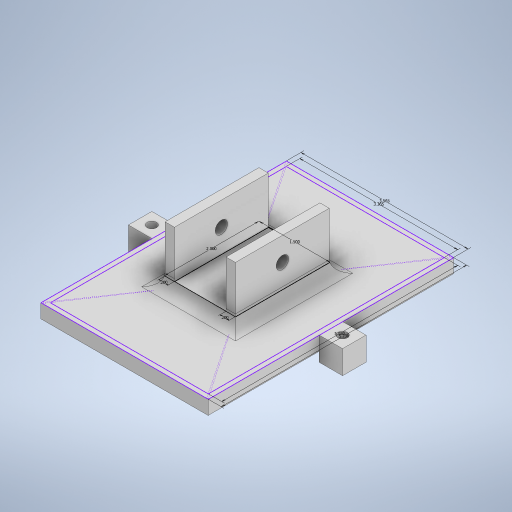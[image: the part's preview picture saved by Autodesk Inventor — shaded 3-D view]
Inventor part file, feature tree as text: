
AUTODESK INVENTOR PART (.ipt)
format: ipt  version: 2024.1 (Build 281209000, 209)  size: 339,968 bytes
history: native  units: in
note: dims shown in document units (in); Inventor stores cm internally (conversion verified against a paired STEP export)
features: extrude x5, sketch x3, projected_geometry x3, hole x2, fillet x1
ambient origin geometry x8: Origin, YZ Plane, XZ Plane, XY Plane, X Axis, Y Axis, Z Axis, Center Point
bodies: Solid1 (feature_tree)
feature tree (14):
  extrude  "Extrusion1"  Depth=2.0in
  extrude  "Extrusion2"  Depth=0.2in
  hole  "Hole1"  [1 undecoded]
  sketch  "Sketch3"  dims[d0=1.5in d1=2.0in]
  extrude  "Extrusion3"  Depth=0.5in
  extrude  "Extrusion4"  Depth=3.3654in
  fillet  "Fillet1"  Radius=5.0299in
  extrude  "Extrusion5"  Depth=5.23in
  hole  "Hole2"  [1 undecoded]
  projected_geometry  "Projected Loop1"
  sketch  "Sketch4"  dims[d2=0.2in d3=0.2in]
  sketch  "Sketch5"  dims[d4=1.0in d5=0.0in d6=0.2in d7=0.0in d8=0.5in d9=0.266in d10=0.75in d11=0.438in d12=0.25in d13=0.5635in d14=1.0in d15=0.8108in d16=3.3654in d17=5.0299in d18=5.23in d19=3.565in d20=0.1in d21=0.0in d22=0.3in d23=0.0in d24=0.25in d25=1.0in d26=0.5in d27=1.0in d28=0.5in d29=0.5in d30=0.0in d31=0.2031in d32=0.75in d33=0.375in d34=0.25in d35=0.5635in d36=1.0in d37=0.8108in]
  projected_geometry  "Projected Loop2"
  projected_geometry  "Projected Loop3"
note: 2 required parameter values undecoded (feature->parameter linkage not recoverable at this tier; creation-order binding heuristic only, values carry confidence <= 0.55)
